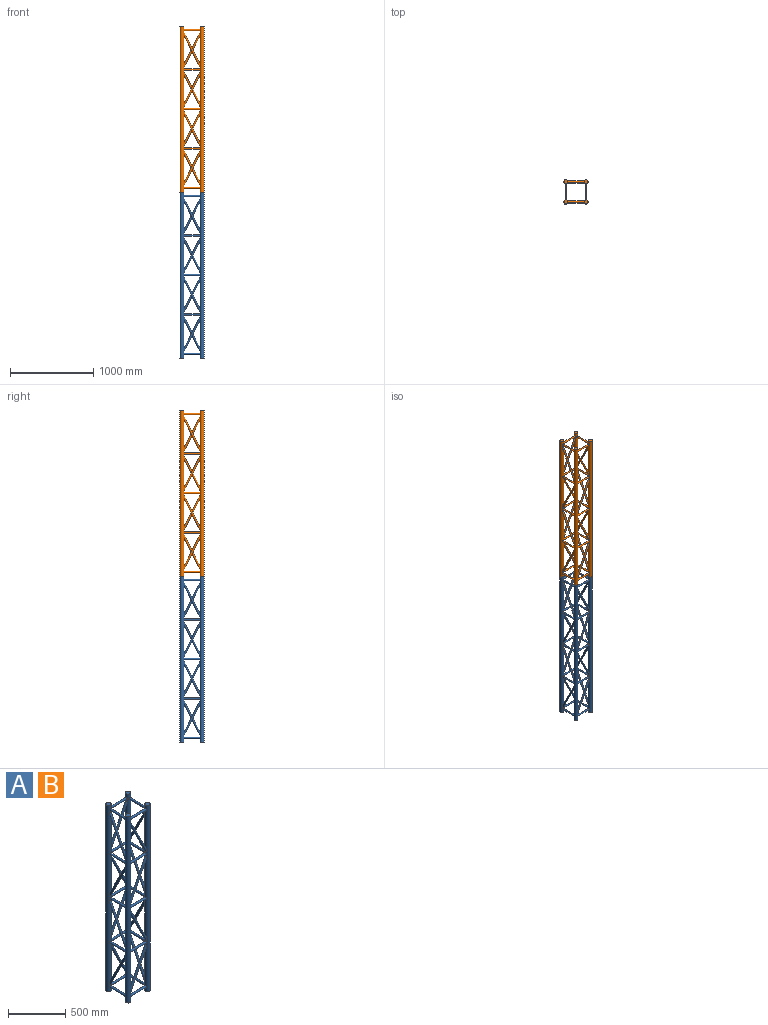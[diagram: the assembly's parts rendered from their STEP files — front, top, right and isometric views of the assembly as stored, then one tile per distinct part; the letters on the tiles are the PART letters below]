
ASSEMBLY  parts=2 mates=1
PART A: 48 faces, bbox 290x290x2000 mm
  f0: cylinder r=24mm len=2000mm, axis (0,0,-1), area 292663.8mm2, adj f1,f2,f3,f4,f5,f6,f7,f8
  f1: plane 48x48mm, normal (0,0,1), area 1809.6mm2, adj f0
  f2: plane 48x48mm, normal (0,0,-1), area 1809.6mm2, adj f0
  f3: cylinder r=10mm len=428.47mm, axis (0,-0.45,0.89), area 27336.7mm2, adj f0,f21
  f4: cylinder r=10mm len=199.34mm, axis (0,1,0), area 12327.8mm2, adj f0,f21
  f5: cylinder r=10mm len=428.46mm, axis (0,0.45,0.89), area 27336.2mm2, adj f0,f21
  f6: cylinder r=10mm len=199.34mm, axis (0,1,0), area 12327.8mm2, adj f0,f21
  f7: cylinder r=10mm len=199.34mm, axis (0,1,0), area 12327.8mm2, adj f0,f21
  f8: cylinder r=10mm len=428.46mm, axis (0,0.45,0.89), area 27336.2mm2, adj f0,f21
  f9: cylinder r=10mm len=199.34mm, axis (0,1,0), area 12327.8mm2, adj f0,f21
  f10: cylinder r=10mm len=428.47mm, axis (0,-0.45,0.89), area 27336.7mm2, adj f0,f21
  f11: cylinder r=10mm len=199.34mm, axis (0,1,0), area 12327.8mm2, adj f0,f21
  f12: cylinder r=10mm len=199.34mm, axis (1,0,0), area 12327.9mm2, adj f0,f33
  f13: cylinder r=10mm len=428.47mm, axis (0.45,0,0.89), area 27336.5mm2, adj f0,f33
  f14: cylinder r=10mm len=199.34mm, axis (1,0,0), area 12327.9mm2, adj f0,f33
  f15: cylinder r=10mm len=428.47mm, axis (-0.45,0,0.89), area 27336.4mm2, adj f0,f33
  f16: cylinder r=10mm len=199.34mm, axis (1,0,0), area 12327.9mm2, adj f0,f33
  f17: cylinder r=10mm len=428.47mm, axis (0.45,0,0.89), area 27336.5mm2, adj f0,f33
  f18: cylinder r=10mm len=199.34mm, axis (1,0,0), area 12327.9mm2, adj f0,f33
  f19: cylinder r=10mm len=428.47mm, axis (-0.45,0,0.89), area 27336.4mm2, adj f0,f33
  f20: cylinder r=10mm len=199.34mm, axis (1,0,0), area 12327.9mm2, adj f0,f33
  f21: cylinder r=24mm len=2000mm, axis (0,0,-1), area 292664.5mm2, adj f3,f4,f5,f6,f7,f8,f9,f10
  f22: plane 48x48mm, normal (0,0,1), area 1809.6mm2, adj f21
  f23: plane 48x48mm, normal (0,0,-1), area 1809.6mm2, adj f21
  f24: cylinder r=10mm len=428.47mm, axis (-0.45,0,0.89), area 27336.6mm2, adj f21,f45
  f25: cylinder r=10mm len=428.46mm, axis (0.45,0,0.89), area 27336.9mm2, adj f21,f45
  f26: cylinder r=10mm len=199.34mm, axis (-1,0,0), area 12328mm2, adj f21,f45
  f27: cylinder r=10mm len=199.34mm, axis (-1,0,0), area 12328mm2, adj f21,f45
  f28: cylinder r=10mm len=428.47mm, axis (-0.45,0,0.89), area 27336.6mm2, adj f21,f45
  f29: cylinder r=10mm len=199.34mm, axis (-1,0,0), area 12328mm2, adj f21,f45
  f30: cylinder r=10mm len=199.34mm, axis (-1,0,0), area 12328mm2, adj f21,f45
  f31: cylinder r=10mm len=428.46mm, axis (0.45,0,0.89), area 27336.9mm2, adj f21,f45
  f32: cylinder r=10mm len=199.34mm, axis (-1,0,0), area 12328mm2, adj f21,f45
  f33: cylinder r=24mm len=2000mm, axis (0,0,-1), area 292664.7mm2, adj f12,f13,f14,f15,f16,f17,f18,f19
  f34: plane 48x48mm, normal (0,0,1), area 1809.6mm2, adj f33
  f35: plane 48x48mm, normal (0,0,-1), area 1809.6mm2, adj f33
  f36: cylinder r=10mm len=428.46mm, axis (0,-0.45,0.89), area 27336.2mm2, adj f33,f45
  f37: cylinder r=10mm len=428.47mm, axis (0,0.45,0.89), area 27336.7mm2, adj f33,f45
  f38: cylinder r=10mm len=199.34mm, axis (0,-1,0), area 12327.8mm2, adj f33,f45
  f39: cylinder r=10mm len=199.34mm, axis (0,-1,0), area 12327.8mm2, adj f33,f45
  f40: cylinder r=10mm len=428.46mm, axis (0,-0.45,0.89), area 27336.2mm2, adj f33,f45
  f41: cylinder r=10mm len=199.34mm, axis (0,-1,0), area 12327.8mm2, adj f33,f45
  f42: cylinder r=10mm len=199.34mm, axis (0,-1,0), area 12327.8mm2, adj f33,f45
  f43: cylinder r=10mm len=428.47mm, axis (0,0.45,0.89), area 27336.7mm2, adj f33,f45
  f44: cylinder r=10mm len=199.34mm, axis (0,-1,0), area 12327.8mm2, adj f33,f45
  f45: cylinder r=24mm len=2000mm, axis (0,0,-1), area 292664.7mm2, adj f24,f25,f26,f27,f28,f29,f30,f31
  f46: plane 48x48mm, normal (0,0,1), area 1809.6mm2, adj f45
  f47: plane 48x48mm, normal (0,0,-1), area 1809.6mm2, adj f45
PART B: same geometry as A
PLACE A t=(-686.88,174.41,-143.53)mm
PLACE B t=(-686.88,174.41,1856.47)mm
MATE fastened A.f21 <-> A.f21  axis (0,0,1) through (-807.88,53.41,1856.47)mm
